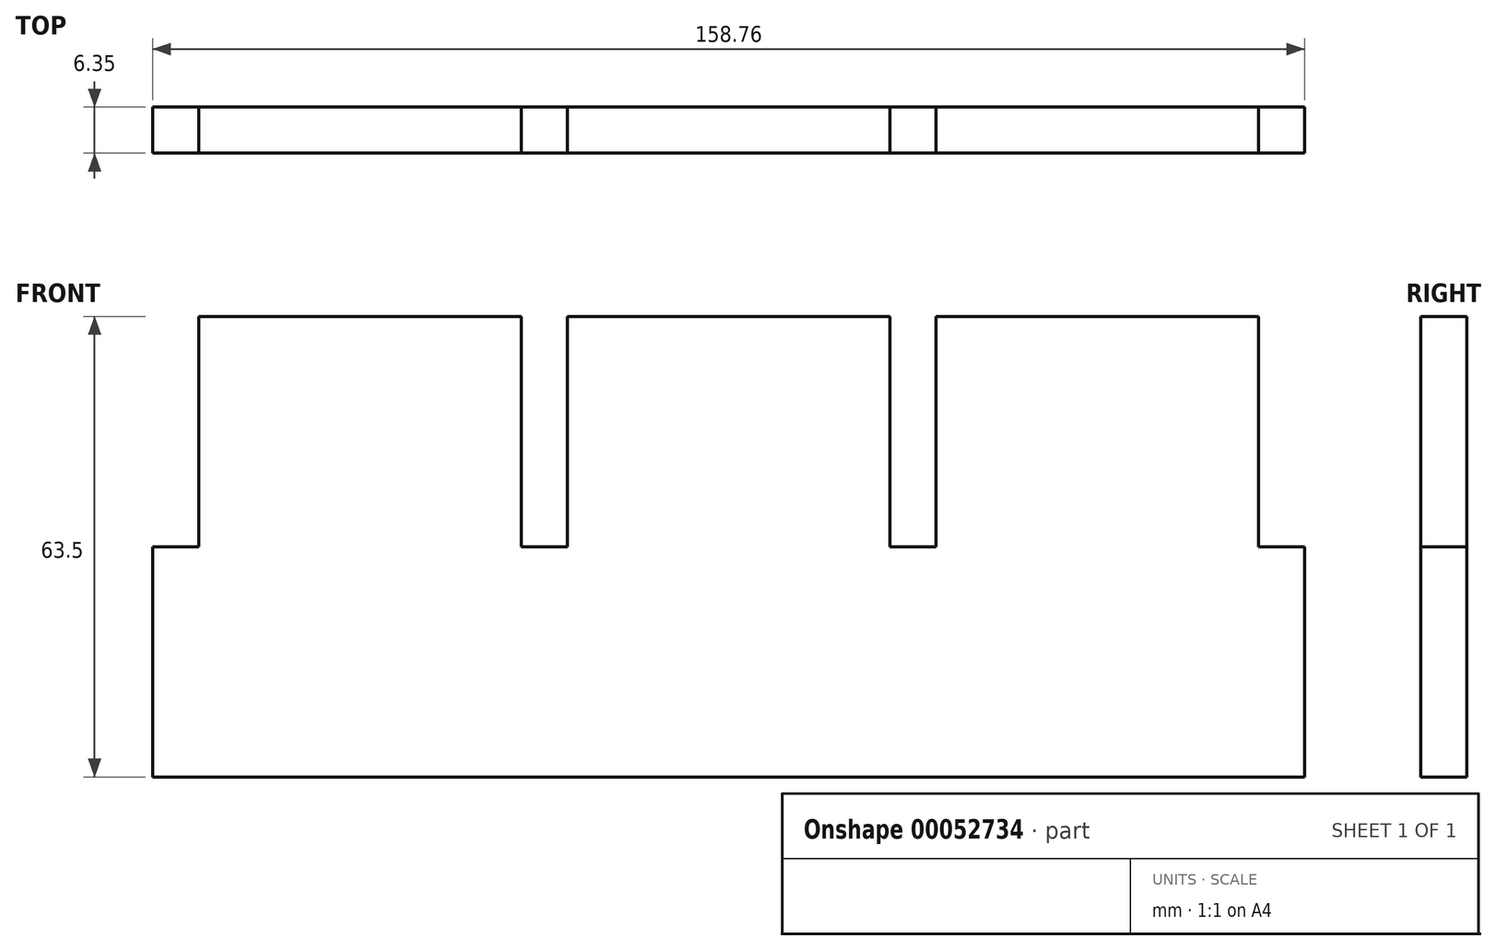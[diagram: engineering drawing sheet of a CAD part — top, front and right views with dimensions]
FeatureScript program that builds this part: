
annotation { "Feature Type Name" : "Feature", "Feature Type Description" : "" }
export const myFeature = defineFeature(function(context is Context, id is Id, definition is map)
    precondition{}
    {
        {
            var Q0;
            Q0=qCreatedBy(makeId("Front.planeOp"),FACE);
            var sketch = newSketch(context, id + "F0", { "sketchPlane" : qUnion([Q0])});
            skLineSegment(sketch, "E0.rect.bottom", {"start": v(-79.38, 31.75) * mm, "end": v(79.37, 31.75) * mm});
            skLineSegment(sketch, "E0.rect.top", {"start": v(-79.38, -31.75) * mm, "end": v(79.38, -31.75) * mm});
            skLineSegment(sketch, "E0.rect.left", {"start": v(-79.38, 31.75) * mm, "end": v(-79.38, -31.75) * mm});
            skLineSegment(sketch, "E0.rect.right", {"start": v(79.37, 31.75) * mm, "end": v(79.38, -31.75) * mm});
            skPoint(sketch, "E0.rect.middle", {"position": v(0, 0) * mm});
            skLineSegment(sketch, "E1", {"start": v(-79.38, 0) * mm, "end": v(79.38, 0) * mm});
            skLineSegment(sketch, "E2", {"start": v(73.03, -31.75) * mm, "end": v(73.03, 0) * mm});
            skLineSegment(sketch, "E3", {"start": v(28.58, -31.75) * mm, "end": v(28.57, 0) * mm});
            skLineSegment(sketch, "E4", {"start": v(22.23, 0) * mm, "end": v(22.23, -31.75) * mm});
            skLineSegment(sketch, "E5", {"start": v(-22.23, 0) * mm, "end": v(-22.23, -31.75) * mm});
            skLineSegment(sketch, "E6", {"start": v(-28.58, 0) * mm, "end": v(-28.58, -31.75) * mm});
            skLineSegment(sketch, "E7", {"start": v(-73.03, 0) * mm, "end": v(-73.03, -31.75) * mm});
            skLineSegment(sketch, "E8", {"start": v(-73.03, 0) * mm, "end": v(-73.03, 31.75) * mm});
            skLineSegment(sketch, "E9", {"start": v(-28.58, 0) * mm, "end": v(-28.58, 31.75) * mm});
            skLineSegment(sketch, "E10", {"start": v(-22.22, 0) * mm, "end": v(-22.23, 31.75) * mm});
            skLineSegment(sketch, "E11", {"start": v(22.22, 0) * mm, "end": v(22.22, 31.75) * mm});
            skLineSegment(sketch, "E12", {"start": v(28.57, 0) * mm, "end": v(28.57, 31.75) * mm});
            skLineSegment(sketch, "E13", {"start": v(73.03, 0) * mm, "end": v(73.03, 31.75) * mm});
            skSolve(sketch);
        }
        {
            var Q0;
            {var subQ0=sQuery(id+"F0.wireOp",EDGE,"E8");Q0=makeQuery(id+"F0.imprint","IMPRINT",FACE,{"disambiguationData":[TD([[makeQuery(id+"F0.imprint","IMPRINT",EDGE,{"derivedFrom":subQ0}),-1.0]])]});}
            var Q1;
            {var subQ0=sQuery(id+"F0.wireOp",EDGE,"E10");Q1=makeQuery(id+"F0.imprint","IMPRINT",FACE,{"disambiguationData":[TD([[makeQuery(id+"F0.imprint","IMPRINT",EDGE,{"derivedFrom":subQ0}),-1.0]])]});}
            var Q2;
            {var subQ0=sQuery(id+"F0.wireOp",EDGE,"E12");Q2=makeQuery(id+"F0.imprint","IMPRINT",FACE,{"disambiguationData":[TD([[makeQuery(id+"F0.imprint","IMPRINT",EDGE,{"derivedFrom":subQ0}),-1.0]])]});}
            var Q3;
            {var subQ0=sQuery(id+"F0.wireOp",EDGE,"E6");Q3=makeQuery(id+"F0.imprint","IMPRINT",FACE,{"disambiguationData":[TD([[makeQuery(id+"F0.imprint","IMPRINT",EDGE,{"derivedFrom":subQ0}),-1.0]])]});}
            var Q4;
            {var subQ0=sQuery(id+"F0.wireOp",EDGE,"E4");Q4=makeQuery(id+"F0.imprint","IMPRINT",FACE,{"disambiguationData":[TD([[makeQuery(id+"F0.imprint","IMPRINT",EDGE,{"derivedFrom":subQ0}),-1.0]])]});}
            var Q5;
            {var subQ0=sQuery(id+"F0.wireOp",EDGE,"E2");Q5=makeQuery(id+"F0.imprint","IMPRINT",FACE,{"disambiguationData":[TD([[makeQuery(id+"F0.imprint","IMPRINT",EDGE,{"derivedFrom":subQ0}),1.0]])]});}
            var Q6;
            {var subQ3=sQuery(id+"F0.wireOp",EDGE,"E7");Q6=makeQuery(id+"F0.imprint","IMPRINT",FACE,{"disambiguationData":[TD([[makeQuery(id+"F0.imprint","IMPRINT",EDGE,{"derivedFrom":subQ3}),-1.0]])]});}
            var Q7;
            {var subQ0=sQuery(id+"F0.wireOp",EDGE,"E5");Q7=makeQuery(id+"F0.imprint","IMPRINT",FACE,{"disambiguationData":[TD([[makeQuery(id+"F0.imprint","IMPRINT",EDGE,{"derivedFrom":subQ0}),-1.0]])]});}
            var Q8;
            {var subQ0=sQuery(id+"F0.wireOp",EDGE,"E3");Q8=makeQuery(id+"F0.imprint","IMPRINT",FACE,{"disambiguationData":[TD([[makeQuery(id+"F0.imprint","IMPRINT",EDGE,{"derivedFrom":subQ0}),1.0]])]});}
            var Q9;
            {var subQ3=sQuery(id+"F0.wireOp",EDGE,"E2");Q9=makeQuery(id+"F0.imprint","IMPRINT",FACE,{"disambiguationData":[TD([[makeQuery(id+"F0.imprint","IMPRINT",EDGE,{"derivedFrom":subQ3}),-1.0]])]});}
            extrude(context, id + "F1", {"entities" : qUnion([Q0, Q1, Q2, Q3, Q4, Q5, Q6, Q7, Q8, Q9]), "depth" : 6.35 * mm});
        }
    });
